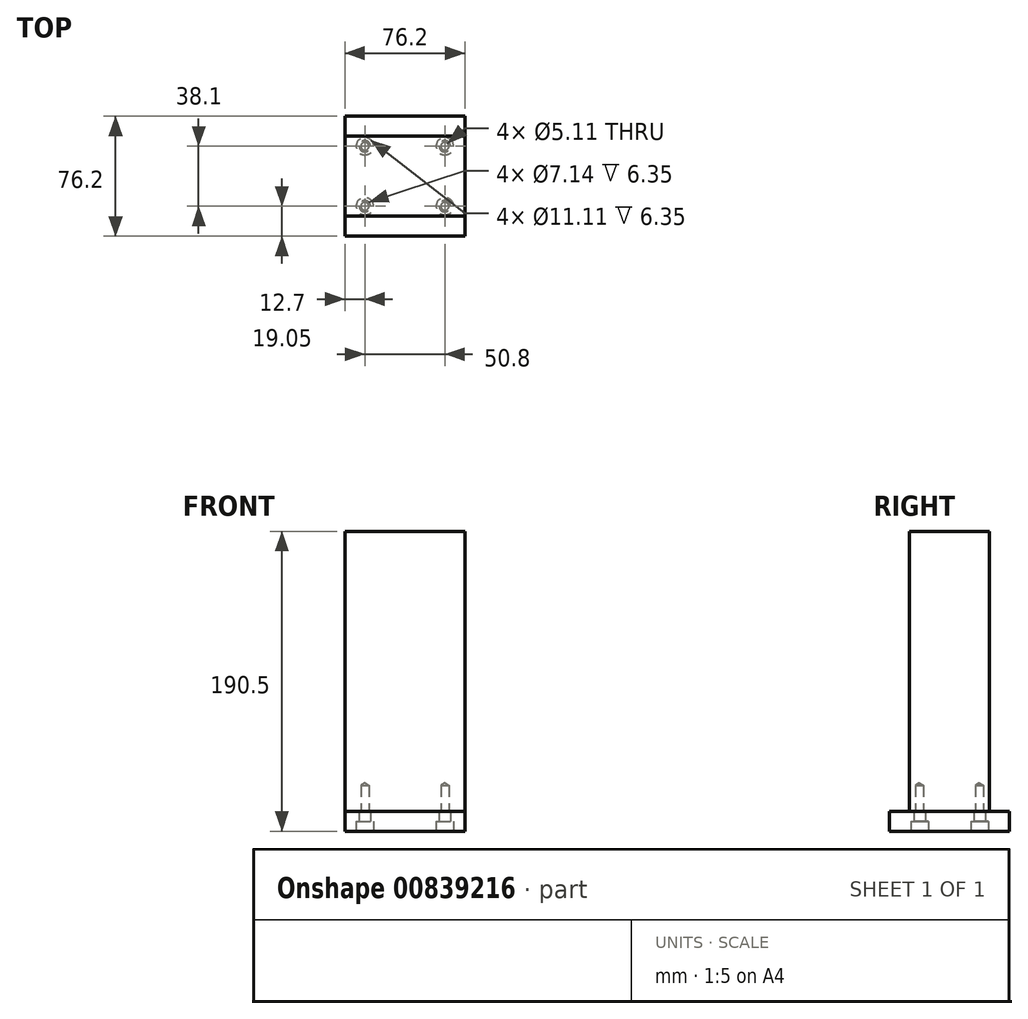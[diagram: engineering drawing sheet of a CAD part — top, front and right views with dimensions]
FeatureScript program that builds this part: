
annotation { "Feature Type Name" : "Feature", "Feature Type Description" : "" }
export const myFeature = defineFeature(function(context is Context, id is Id, definition is map)
    precondition{}
    {
        {
            var Q0;
            Q0=qCreatedBy(makeId("Top.planeOp"),FACE);
            var sketch = newSketch(context, id + "F0", { "sketchPlane" : qUnion([Q0])});
            skLineSegment(sketch, "E0.bottom", {"start": v(38.1, -38.1) * mm, "end": v(-38.1, -38.1) * mm});
            skLineSegment(sketch, "E0.top", {"start": v(38.1, 38.1) * mm, "end": v(-38.1, 38.1) * mm});
            skLineSegment(sketch, "E0.left", {"start": v(38.1, -38.1) * mm, "end": v(38.1, 38.1) * mm});
            skLineSegment(sketch, "E0.right", {"start": v(-38.1, -38.1) * mm, "end": v(-38.1, 38.1) * mm});
            skPoint(sketch, "E0.middle", {"position": v(0, 0) * mm});
            skSolve(sketch);
        }
        {
            var Q0;
            Q0=qSketchRegion(id+"F0",true);
            extrude(context, id + "F1", {"entities" : qUnion([Q0]), "depth" : 12.7 * mm, "offsetDistance" : 25.4 * mm});
        }
        {
            var Q0;
            Q0=makeQuery(id+"F1.opExtrude","CAP_FACE",FACE,{"disambiguationData":[OSD([sQuery(id+"F0.wireOp",EDGE,"E0.bottom"),sQuery(id+"F0.wireOp",EDGE,"E0.top"),sQuery(id+"F0.wireOp",EDGE,"E0.left"),sQuery(id+"F0.wireOp",EDGE,"E0.right")])],"isStart":false});
            var sketch = newSketch(context, id + "F2", { "sketchPlane" : qUnion([Q0])});
            skLineSegment(sketch, "E1.bottom", {"start": v(38.1, -25.4) * mm, "end": v(-38.1, -25.4) * mm});
            skLineSegment(sketch, "E1.top", {"start": v(38.1, 25.4) * mm, "end": v(-38.1, 25.4) * mm});
            skLineSegment(sketch, "E1.left", {"start": v(38.1, -25.4) * mm, "end": v(38.1, 25.4) * mm});
            skLineSegment(sketch, "E1.right", {"start": v(-38.1, -25.4) * mm, "end": v(-38.1, 25.4) * mm});
            skPoint(sketch, "E1.middle", {"position": v(0, 0) * mm});
            skSolve(sketch);
        }
        {
            var Q0;
            Q0=qSketchRegion(id+"F2",true);
            extrude(context, id + "F3", {"entities" : qUnion([Q0]), "depth" : 177.8 * mm, "offsetDistance" : 25.4 * mm});
        }
        {
            var Q0;
            Q0=makeQuery(id+"F1.opExtrude","CAP_FACE",FACE,{"disambiguationData":[OSD([sQuery(id+"F0.wireOp",EDGE,"E0.bottom"),sQuery(id+"F0.wireOp",EDGE,"E0.top"),sQuery(id+"F0.wireOp",EDGE,"E0.left"),sQuery(id+"F0.wireOp",EDGE,"E0.right")])],"isStart":true});
            var sketch = newSketch(context, id + "F4", { "sketchPlane" : qUnion([Q0])});
            skLineSegment(sketch, "E2.bottom", {"start": v(-25.4, 19.05) * mm, "end": v(25.4, 19.05) * mm, "construction": true});
            skLineSegment(sketch, "E2.top", {"start": v(-25.4, -19.05) * mm, "end": v(25.4, -19.05) * mm, "construction": true});
            skLineSegment(sketch, "E2.left", {"start": v(-25.4, 19.05) * mm, "end": v(-25.4, -19.05) * mm, "construction": true});
            skLineSegment(sketch, "E2.right", {"start": v(25.4, 19.05) * mm, "end": v(25.4, -19.05) * mm, "construction": true});
            skPoint(sketch, "E2.middle", {"position": v(0, 0) * mm});
            skPoint(sketch, "E3", {"position": v(0, 19.05) * mm});
            skPoint(sketch, "E4", {"position": v(0, -19.05) * mm});
            skPoint(sketch, "E5", {"position": v(6.35, 19.05) * mm});
            skPoint(sketch, "E6", {"position": v(-6.35, -19.05) * mm});
            skSolve(sketch);
        }
        {
            var Q0;
            Q0=sQuery(id+"F4.wireOp",VERTEX,"E2.left.end");
            var Q1;
            Q1=sQuery(id+"F4.wireOp",VERTEX,"E2.left.start");
            var Q2;
            Q2=sQuery(id+"F4.wireOp",VERTEX,"E2.top.end");
            var Q3;
            Q3=sQuery(id+"F4.wireOp",VERTEX,"E2.bottom.end");
            var Q4;
            Q4=makeQuery(id+"F1.opExtrude","SWEPT_BODY",BODY,{"disambiguationData":[OSD([sQuery(id+"F0.wireOp",EDGE,"E0.bottom"),sQuery(id+"F0.wireOp",EDGE,"E0.top"),sQuery(id+"F0.wireOp",EDGE,"E0.left"),sQuery(id+"F0.wireOp",EDGE,"E0.right")])]});
            hole(context, id + "F5", {"style" : HoleStyle.C_BORE, "endStyle" : HoleEndStyle.THROUGH, "holeDiameter" : 7.14 * mm, "cBoreDiameter" : 11.1 * mm, "cBoreDepth" : 6.35 * mm, "majorDiameter" : 6.35 * mm, "isTappedThrough" : true, "tappedDepth" : 12.7 * mm, "tapClearance" : 3, "locations" : qUnion([Q0, Q1, Q2, Q3]), "scope" : qUnion([Q4])});
        }
        {
            var Q0;
            Q0=sQuery(id+"F4.wireOp",VERTEX,"E2.top.end");
            var Q1;
            Q1=sQuery(id+"F4.wireOp",VERTEX,"E2.bottom.end");
            var Q2;
            Q2=sQuery(id+"F4.wireOp",VERTEX,"E2.left.end");
            var Q3;
            Q3=sQuery(id+"F4.wireOp",VERTEX,"E2.left.start");
            var Q4;
            Q4=makeQuery(id+"F3.opExtrude","SWEPT_BODY",BODY,{"disambiguationData":[OSD([sQuery(id+"F2.wireOp",EDGE,"E1.bottom"),sQuery(id+"F2.wireOp",EDGE,"E1.top"),sQuery(id+"F2.wireOp",EDGE,"E1.left"),sQuery(id+"F2.wireOp",EDGE,"E1.right")])]});
            hole(context, id + "F6", {"style" : HoleStyle.SIMPLE, "endStyle" : HoleEndStyle.BLIND, "standardTappedOrClearance" : lookupTablePath({ "fit" : "Normal (ASME)", "standard" : "ANSI", "engagement" : "75%", "pitch" : "20 tpi", "size" : "1/4", "type" : "Tapped" }), "standardBlindInLast" : lookupTablePath({ "fit" : "Free", "standard" : "ANSI", "engagement" : "75%", "pitch" : "20 tpi", "size" : "1/4", "type" : "Tapped" }), "holeDiameter" : 5.1 * mm, "majorDiameter" : 6.35 * mm, "showTappedDepth" : true, "holeDepth" : 16.51 * mm, "isTappedThrough" : true, "tappedDepth" : 12.7 * mm, "tapClearance" : 3, "locations" : qUnion([Q0, Q1, Q2, Q3]), "scope" : qUnion([Q4])});
        }
    });
